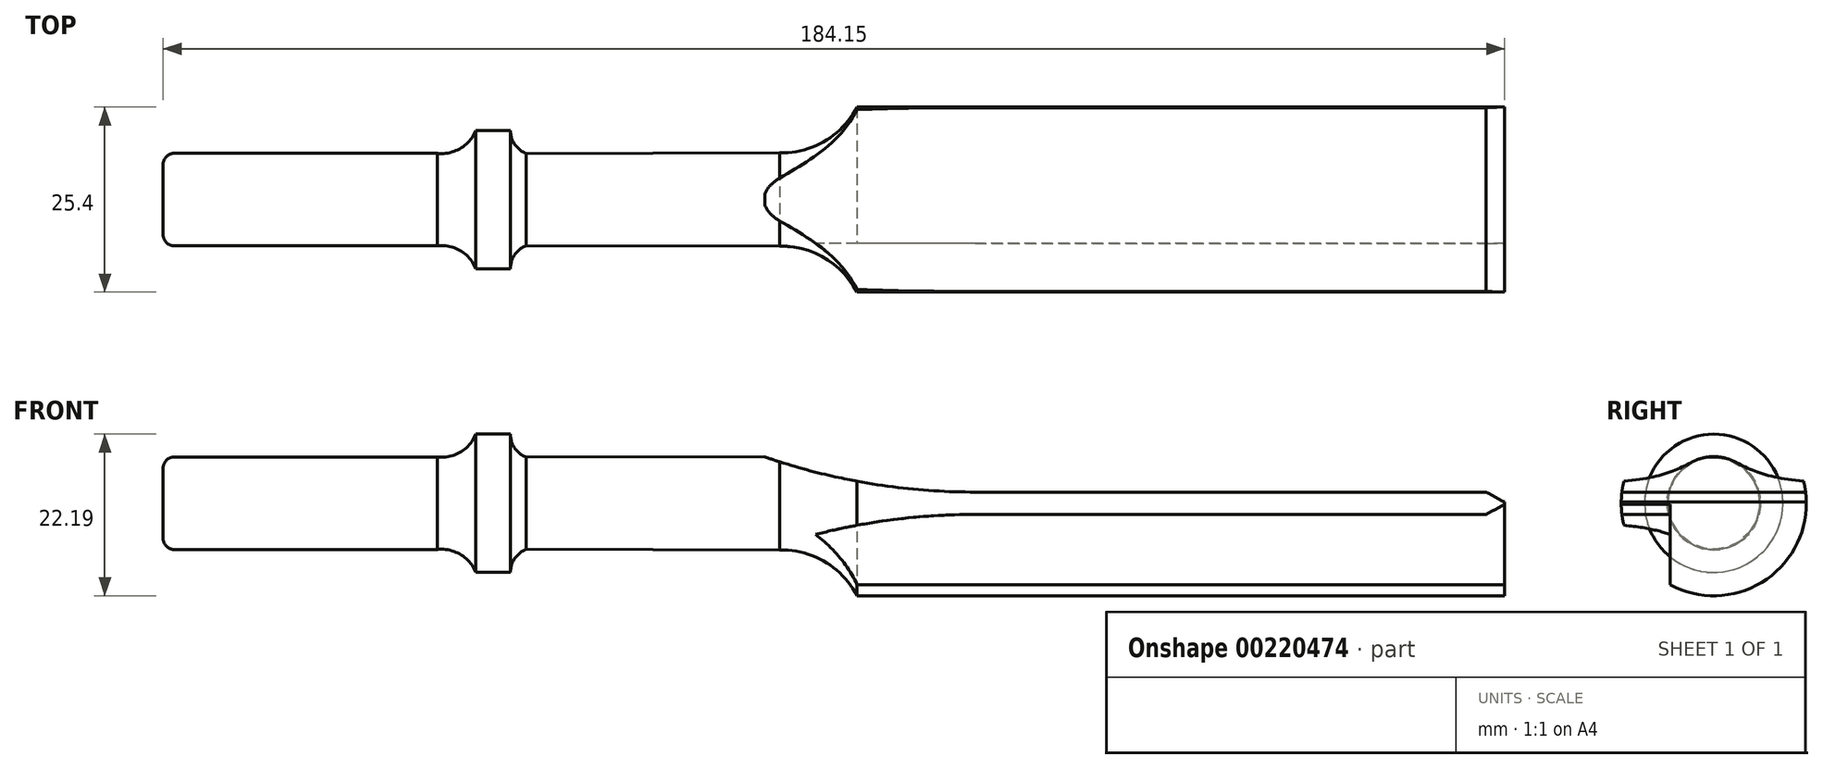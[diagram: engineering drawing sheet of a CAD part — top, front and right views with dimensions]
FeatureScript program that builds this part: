
annotation { "Feature Type Name" : "Feature", "Feature Type Description" : "" }
export const myFeature = defineFeature(function(context is Context, id is Id, definition is map)
    precondition{}
    {
        {
            var Q0;
            Q0=qCreatedBy(makeId("Top.planeOp"),FACE);
            var sketch = newSketch(context, id + "F0", { "sketchPlane" : qUnion([Q0])});
            skLineSegment(sketch, "E0", {"start": v(-86.54, 6) * mm, "end": v(97.6, 6) * mm});
            skLineSegment(sketch, "E1", {"start": v(97.6, 6) * mm, "end": v(97.6, 18.7) * mm});
            skLineSegment(sketch, "E2", {"start": v(97.6, 18.7) * mm, "end": v(8.7, 18.7) * mm});
            skLineSegment(sketch, "E3", {"start": v(-86.54, 6) * mm, "end": v(-86.54, 10.83) * mm});
            skLineSegment(sketch, "E4", {"start": v(-85.02, 12.35) * mm, "end": v(-47.75, 12.35) * mm});
            skLineSegment(sketch, "E5", {"start": v(8.7, 12.43) * mm, "end": v(8.7, 12.32) * mm});
            skLineSegment(sketch, "E6", {"start": v(-43.63, 15.5) * mm, "end": v(-38.88, 15.5) * mm});
            skLineSegment(sketch, "E7", {"start": v(-36.7, 12.33) * mm, "end": v(-1.33, 12.4) * mm});
            skPoint(sketch, "E8.visualSharp", {"position": v(8.7, 12.43) * mm});
            skArc(sketch, "E9", {"start": v(-38.88, 15.5) * mm, "mid": v(-38.28, 13.58) * mm, "end": v(-36.7, 12.33) * mm});
            skArc(sketch, "E10", {"start": v(-48.88, 12.35) * mm, "mid": v(-45.72, 13.04) * mm, "end": v(-43.63, 15.5) * mm});
            skArc(sketch, "E11", {"start": v(-1.92, 12.4) * mm, "mid": v(4.3, 14.03) * mm, "end": v(8.7, 18.7) * mm});
            skPoint(sketch, "E12.visualSharp", {"position": v(-86.54, 12.35) * mm});
            skArc(sketch, "E12.filletArc", {"start": v(-85.02, 12.35) * mm, "mid": v(-86.1, 11.9) * mm, "end": v(-86.54, 10.83) * mm});
            skPoint(sketch, "E13.visualSharp", {"position": v(-86.54, 6) * mm});
            skSolve(sketch);
        }
        {
            var Q0;
            Q0=makeQuery(id+"F0.imprint","IMPRINT",FACE,{"disambiguationData":[TD([[makeQuery(id+"F0.imprint","IMPRINT",EDGE,{"derivedFrom":sQuery(id+"F0.wireOp",EDGE,"E0")}),1.0]])]});
            var Q1;
            Q1=sQuery(id+"F0.wireOp",EDGE,"E0");
            revolve(context, id + "F1", {"entities" : qUnion([Q0]), "axis" : qUnion([Q1]), "revolveType" : RevolveType.FULL});
        }
        {
            var Q0;
            Q0=qCreatedBy(makeId("Front.planeOp"),FACE);
            var sketch = newSketch(context, id + "F2", { "sketchPlane" : qUnion([Q0])});
            skLineSegment(sketch, "E14", {"start": v(208.38, 0) * mm, "end": v(208.38, 94.63) * mm, "construction": true});
            skLineSegment(sketch, "E15", {"start": v(208.38, 0) * mm, "end": v(-230.2, 0) * mm, "construction": true});
            skLineSegment(sketch, "E16", {"start": v(0, 0) * mm, "end": v(0, 6.35) * mm, "construction": true});
            skPoint(sketch, "E17", {"position": v(0, 13.84) * mm});
            skLineSegment(sketch, "E18", {"start": v(208.38, 13.84) * mm, "end": v(253.14, 13.84) * mm, "construction": true});
            skLineSegment(sketch, "E19", {"start": v(-3.93, 13.84) * mm, "end": v(-228.26, 13.84) * mm, "construction": true});
            skArc(sketch, "E20", {"start": v(-3.93, 6.35) * mm, "mid": v(10.3, 2.75) * mm, "end": v(24.95, 1.54) * mm});
            skPoint(sketch, "E21.orphan", {"position": v(564.09, 0) * mm});
            skLineSegment(sketch, "E22.0", {"start": v(208.38, 6.35) * mm, "end": v(-230.2, 6.35) * mm, "construction": true});
            skPoint(sketch, "E23", {"position": v(97.67, 27.84) * mm});
            skLineSegment(sketch, "E24.0", {"start": v(-3.93, 6.35) * mm, "end": v(-3.93, 27.84) * mm});
            skPoint(sketch, "E25", {"position": v(-3.93, 6.35) * mm});
            skLineSegment(sketch, "E26", {"start": v(24.95, 1.54) * mm, "end": v(95.05, 1.54) * mm});
            skPoint(sketch, "E27.orphan", {"position": v(24.95, 1.54) * mm});
            skPoint(sketch, "E28.MirrorCS.start.orphan", {"position": v(-3.93, -3.28) * mm});
            skLineSegment(sketch, "E29", {"start": v(-85.17, -6.32) * mm, "end": v(-3.83, -6.32) * mm, "construction": true});
            skArc(sketch, "E30.MirrorCS", {"start": v(-3.93, -6.35) * mm, "mid": v(10.3, -2.75) * mm, "end": v(24.95, -1.54) * mm});
            skLineSegment(sketch, "E31.MirrorCS", {"start": v(24.95, -1.54) * mm, "end": v(95.05, -1.54) * mm});
            skLineSegment(sketch, "E32", {"start": v(97.67, 27.84) * mm, "end": v(113.44, 27.84) * mm});
            skPoint(sketch, "E32.startSnap0", {"position": v(-3.93, 27.84) * mm});
            skLineSegment(sketch, "E33", {"start": v(113.44, 27.84) * mm, "end": v(113.44, 10.6) * mm});
            skLineSegment(sketch, "E34", {"start": v(100.47, 1.54) * mm, "end": v(113.44, 10.6) * mm});
            skLineSegment(sketch, "E35", {"start": v(97.88, 0) * mm, "end": v(100.47, 1.54) * mm});
            skLineSegment(sketch, "E36.MirrorCS", {"start": v(113.44, -27.84) * mm, "end": v(113.44, -10.6) * mm});
            skLineSegment(sketch, "E37.MirrorCS", {"start": v(100.47, -1.54) * mm, "end": v(113.44, -10.6) * mm});
            skLineSegment(sketch, "E38.MirrorCS", {"start": v(0, 0) * mm, "end": v(0, -6.32) * mm, "construction": true});
            skLineSegment(sketch, "E39.MirrorCS", {"start": v(95.05, -1.54) * mm, "end": v(97.88, 0) * mm});
            skLineSegment(sketch, "E40.MirrorCS", {"start": v(97.88, 0) * mm, "end": v(100.47, -1.54) * mm});
            skPoint(sketch, "E41.orphan", {"position": v(0, 93.07) * mm});
            skPoint(sketch, "E42.orphan", {"position": v(0, 27.84) * mm});
            skLineSegment(sketch, "E43", {"start": v(97.67, 27.84) * mm, "end": v(-3.93, 27.84) * mm});
            skPoint(sketch, "E44.MirrorCS.end.orphan", {"position": v(113.44, -27.84) * mm});
            skPoint(sketch, "E44.MirrorCS.start.orphan", {"position": v(0, -27.84) * mm});
            skLineSegment(sketch, "E45", {"start": v(113.44, -27.84) * mm, "end": v(-3.93, -27.84) * mm});
            skPoint(sketch, "E46.orphan", {"position": v(100.47, -1.54) * mm});
            skLineSegment(sketch, "E47.trimOffspring", {"start": v(107.3, -6.32) * mm, "end": v(195.27, -6.32) * mm, "construction": true});
            skLineSegment(sketch, "E48.MirrorCS", {"start": v(208.38, -6.35) * mm, "end": v(-230.2, -6.35) * mm, "construction": true});
            skLineSegment(sketch, "E49.MirrorCS", {"start": v(0, 0) * mm, "end": v(0, -6.35) * mm, "construction": true});
            skLineSegment(sketch, "E50", {"start": v(95.05, 1.54) * mm, "end": v(97.88, 0) * mm});
            skPoint(sketch, "E51.orphan", {"position": v(-3.93, 55.68) * mm});
            skPoint(sketch, "E52.orphan", {"position": v(-3.93, -55.68) * mm});
            skPoint(sketch, "E53.trimOffspring.end.orphan", {"position": v(0, -93.07) * mm});
            skPoint(sketch, "E54.trimOffspring.end.orphan", {"position": v(97.45, 55.68) * mm});
            skLineSegment(sketch, "E55.MirrorCS", {"start": v(208.38, 0) * mm, "end": v(208.38, -94.63) * mm, "construction": true});
            skLineSegment(sketch, "E56.MirrorCS", {"start": v(208.38, -13.84) * mm, "end": v(253.14, -13.84) * mm, "construction": true});
            skLineSegment(sketch, "E57.trimOffspring", {"start": v(-3.93, -6.32) * mm, "end": v(-3.93, -27.84) * mm});
            skPoint(sketch, "E58.MirrorCS.start.orphan", {"position": v(-3.93, 0) * mm});
            skSolve(sketch);
        }
        {
            var Q0;
            Q0=makeQuery(id+"F2.imprint","IMPRINT",FACE,{"disambiguationData":[TD([[makeQuery(id+"F2.imprint","IMPRINT",EDGE,{"derivedFrom":sQuery(id+"F2.wireOp",EDGE,"E20")}),1.0]])]});
            var Q1;
            {var subQ1=sQuery(id+"F2.wireOp",EDGE,"E30.MirrorCS");Q1=makeQuery(id+"F2.imprint","IMPRINT",FACE,{"disambiguationData":[TD([[makeQuery(id+"F2.imprint","IMPRINT",EDGE,{"derivedFrom":subQ1}),-1.0]])]});}
            extrude(context, id + "F3", {"entities" : qUnion([Q0, Q1]), "operationType" : NewBodyOperationType.REMOVE, "oppositeDirection" : true, "depth" : 63.5 * mm});
        }
        {
            var Q0;
            Q0 = qSketchRegion(id + "F2", true);
            extrude(context, id + "F4", {"entities" : qUnion([Q0]), "operationType" : NewBodyOperationType.REMOVE, "depth" : 25.4 * mm});
        }
    });
